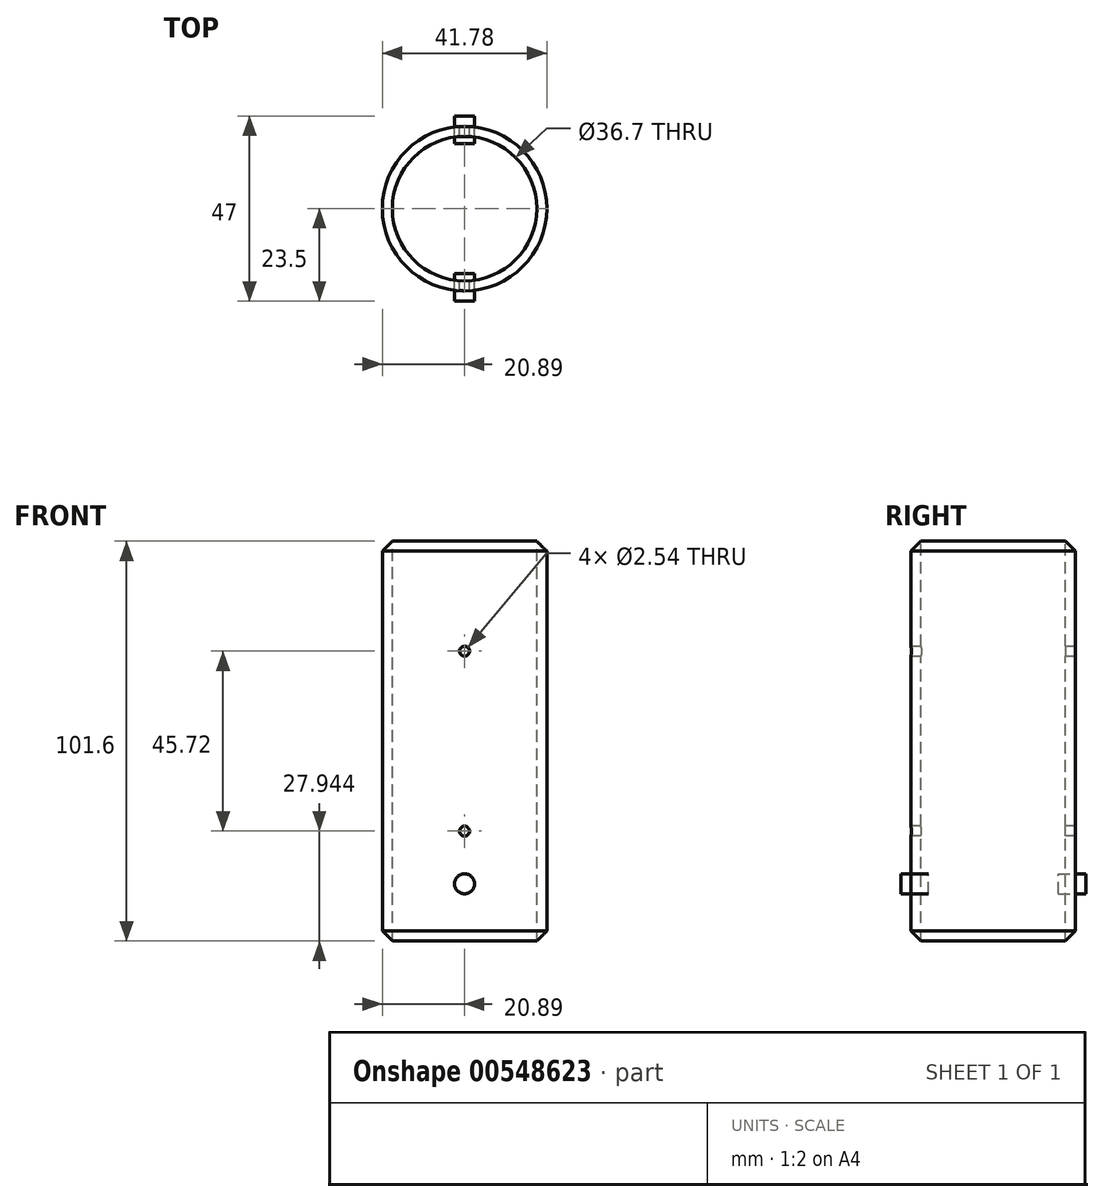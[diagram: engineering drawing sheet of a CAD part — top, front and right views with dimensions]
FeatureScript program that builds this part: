
annotation { "Feature Type Name" : "Feature", "Feature Type Description" : "" }
export const myFeature = defineFeature(function(context is Context, id is Id, definition is map)
    precondition{}
    {
        {
            var Q0;
            Q0=qCreatedBy(makeId("Front.planeOp"),FACE);
            var sketch = newSketch(context, id + "F0", { "sketchPlane" : qUnion([Q0])});
            skLineSegment(sketch, "E0", {"start": v(18.35, 74.36) * mm, "end": v(18.35, -27.24) * mm});
            skLineSegment(sketch, "E1", {"start": v(18.35, -27.24) * mm, "end": v(20.9, -24.7) * mm});
            skLineSegment(sketch, "E2", {"start": v(20.9, -24.7) * mm, "end": v(20.9, 71.82) * mm});
            skLineSegment(sketch, "E3", {"start": v(20.9, 71.82) * mm, "end": v(18.35, 74.36) * mm});
            skSolve(sketch);
        }
        {
            var Q0;
            Q0=qCreatedBy(makeId("Front.planeOp"),FACE);
            var sketch = newSketch(context, id + "F1", { "sketchPlane" : qUnion([Q0])});
            skLineSegment(sketch, "E4", {"start": v(0, 75.83) * mm, "end": v(0, -28.92) * mm});
            skSolve(sketch);
        }
        {
            var Q0;
            Q0=makeQuery(id+"F0.imprint","IMPRINT",FACE,{"disambiguationData":[TD([[makeQuery(id+"F0.imprint","IMPRINT",EDGE,{"derivedFrom":sQuery(id+"F0.wireOp",EDGE,"E0")}),1.0]])]});
            var Q1;
            Q1=sQuery(id+"F1.wireOp",EDGE,"E4");
            revolve(context, id + "F2", {"entities" : qUnion([Q0]), "axis" : qUnion([Q1]), "revolveType" : RevolveType.FULL});
        }
        {
            var Q0;
            Q0=qCreatedBy(makeId("Front.planeOp"),FACE);
            var sketch = newSketch(context, id + "F3", { "sketchPlane" : qUnion([Q0])});
            skCircle(sketch, "E5", {"center": v(0, -12.7) * mm, "radius": 2.54 * mm});
            skSolve(sketch);
        }
        {
            var Q0;
            Q0 = qSketchRegion(id + "F3", true);
            extrude(context, id + "F4", {"entities" : qUnion([Q0]), "endBound" : BoundingType.SYMMETRIC, "depth" : 47 * mm, "offsetDistance" : 25.4 * mm});
        }
        {
            var Q0;
            Q0 = qSketchRegion(id + "F3", true);
            extrude(context, id + "F5", {"entities" : qUnion([Q0]), "operationType" : NewBodyOperationType.REMOVE, "endBound" : BoundingType.SYMMETRIC, "depth" : 33.02 * mm, "offsetDistance" : 25.4 * mm});
        }
        {
            var Q0;
            Q0=qCreatedBy(makeId("Front.planeOp"),FACE);
            var sketch = newSketch(context, id + "F6", { "sketchPlane" : qUnion([Q0])});
            skCircle(sketch, "E6", {"center": v(0, 46.42) * mm, "radius": 1.27 * mm});
            skSolve(sketch);
        }
        {
            var Q0;
            Q0 = qSketchRegion(id + "F6", true);
            var Q1;
            Q1=sQuery(id+"F6.wireOp",EDGE,"E6");
            extrude(context, id + "F7", {"entities" : qUnion([Q0]), "operationType" : NewBodyOperationType.REMOVE, "surfaceEntities" : qUnion([Q1]), "endBound" : BoundingType.SYMMETRIC, "depth" : 101.6 * mm, "offsetDistance" : 25.4 * mm});
        }
        {
            var Q0;
            Q0=qCreatedBy(makeId("Front.planeOp"),FACE);
            var sketch = newSketch(context, id + "F8", { "sketchPlane" : qUnion([Q0])});
            skCircle(sketch, "E7", {"center": v(0, 0.7) * mm, "radius": 1.27 * mm});
            skSolve(sketch);
        }
        {
            var Q0;
            Q0 = qSketchRegion(id + "F8", true);
            extrude(context, id + "F9", {"entities" : qUnion([Q0]), "operationType" : NewBodyOperationType.REMOVE, "endBound" : BoundingType.SYMMETRIC, "oppositeDirection" : true, "depth" : 127 * mm, "offsetDistance" : 25.4 * mm});
        }
    });
